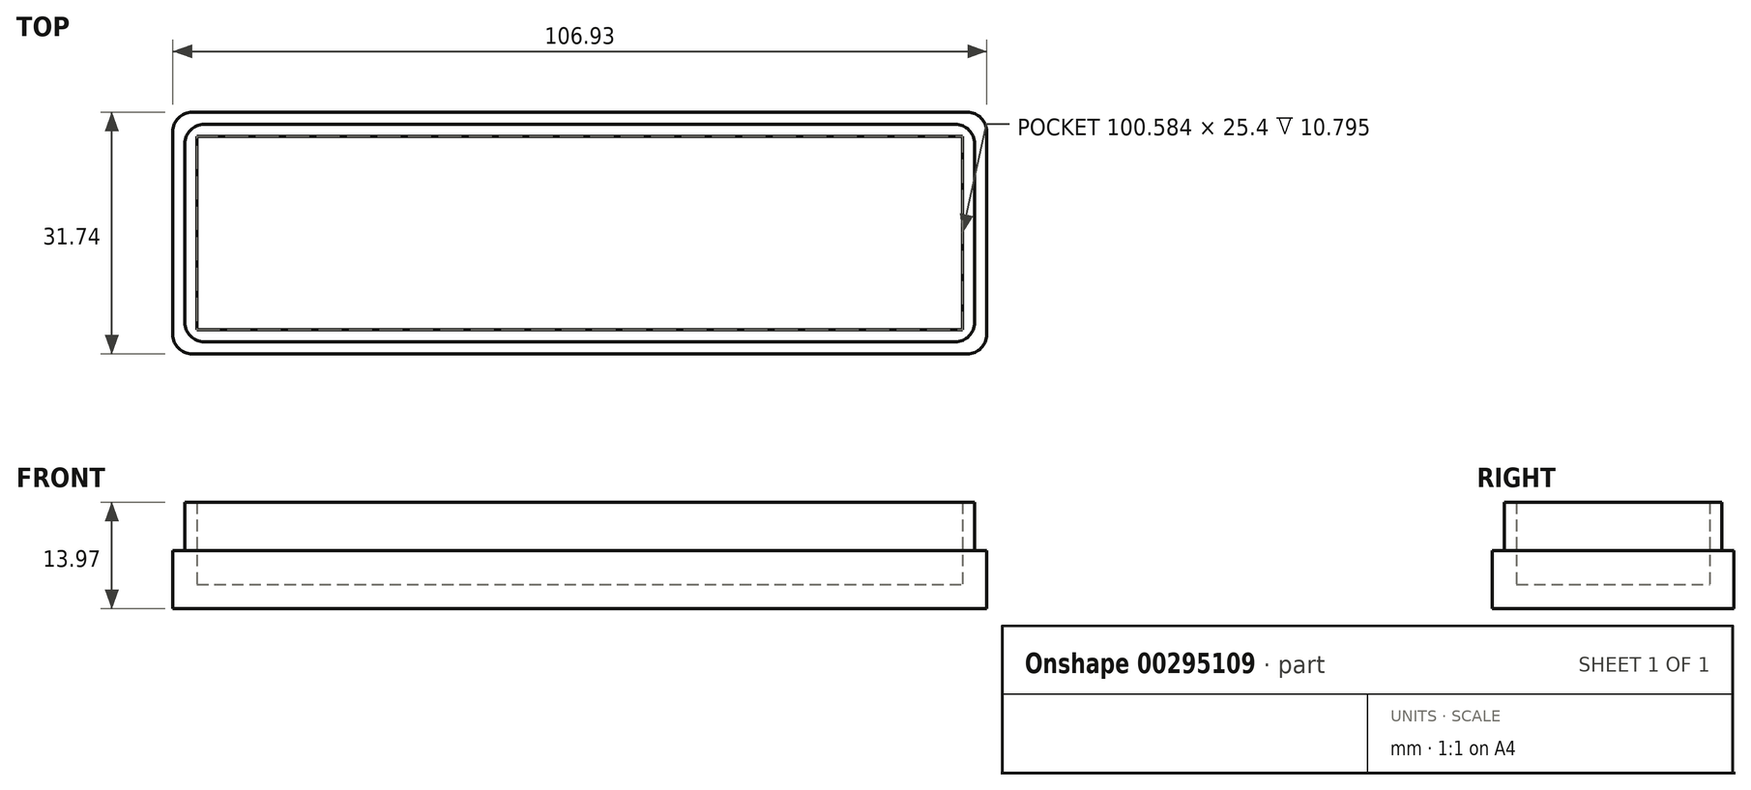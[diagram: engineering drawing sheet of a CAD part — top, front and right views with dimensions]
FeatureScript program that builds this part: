
annotation { "Feature Type Name" : "Feature", "Feature Type Description" : "" }
export const myFeature = defineFeature(function(context is Context, id is Id, definition is map)
    precondition{}
    {
        {
            var Q0;
            Q0=qCreatedBy(makeId("Top.planeOp"),FACE);
            var sketch = newSketch(context, id + "F0", { "sketchPlane" : qUnion([Q0])});
            skLineSegment(sketch, "E0.bottom", {"start": v(0, 0) * mm, "end": v(100.58, 0) * mm});
            skLineSegment(sketch, "E0.top", {"start": v(0, 25.4) * mm, "end": v(100.58, 25.4) * mm});
            skLineSegment(sketch, "E0.left", {"start": v(0, 0) * mm, "end": v(0, 25.4) * mm});
            skLineSegment(sketch, "E0.right", {"start": v(100.58, 0) * mm, "end": v(100.58, 25.4) * mm});
            skLineSegment(sketch, "E1.bottom", {"start": v(-3.18, 28.58) * mm, "end": v(103.76, 28.58) * mm});
            skLineSegment(sketch, "E1.top", {"start": v(-3.18, -3.18) * mm, "end": v(103.76, -3.18) * mm});
            skLineSegment(sketch, "E1.left", {"start": v(-3.18, 28.58) * mm, "end": v(-3.17, -3.18) * mm});
            skLineSegment(sketch, "E1.right", {"start": v(103.76, 28.58) * mm, "end": v(103.76, -3.18) * mm});
            skSolve(sketch);
        }
        {
            var Q0;
            Q0=makeQuery(id+"F0.imprint","IMPRINT",FACE,{"disambiguationData":[TD([[makeQuery(id+"F0.imprint","IMPRINT",EDGE,{"derivedFrom":sQuery(id+"F0.wireOp",EDGE,"E0.bottom")}),-1.0]])]});
            extrude(context, id + "F1", {"entities" : qUnion([Q0]), "depth" : 13.97 * mm});
        }
        {
            var Q0;
            Q0=makeQuery(id+"F0.imprint","IMPRINT",FACE,{"disambiguationData":[TD([[makeQuery(id+"F0.imprint","IMPRINT",EDGE,{"derivedFrom":sQuery(id+"F0.wireOp",EDGE,"E0.bottom")}),1.0]])]});
            extrude(context, id + "F2", {"entities" : qUnion([Q0]), "operationType" : NewBodyOperationType.ADD, "depth" : 3.17 * mm});
        }
        {
            var Q0;
            Q0=makeQuery(id+"F1.opExtrude","CAP_FACE",FACE,{"disambiguationData":[OSD([sQuery(id+"F0.wireOp",EDGE,"E0.bottom"),sQuery(id+"F0.wireOp",EDGE,"E0.top"),sQuery(id+"F0.wireOp",EDGE,"E0.left"),sQuery(id+"F0.wireOp",EDGE,"E0.right"),sQuery(id+"F0.wireOp",EDGE,"E1.bottom"),sQuery(id+"F0.wireOp",EDGE,"E1.top"),sQuery(id+"F0.wireOp",EDGE,"E1.left"),sQuery(id+"F0.wireOp",EDGE,"E1.right")])],"isStart":false});
            var sketch = newSketch(context, id + "F3", { "sketchPlane" : qUnion([Q0])});
            skLineSegment(sketch, "E2.bottom", {"start": v(-1.59, -1.59) * mm, "end": v(102.17, -1.59) * mm});
            skLineSegment(sketch, "E2.top", {"start": v(-1.59, 26.99) * mm, "end": v(102.17, 26.99) * mm});
            skLineSegment(sketch, "E2.left", {"start": v(-1.59, -1.59) * mm, "end": v(-1.59, 26.99) * mm});
            skLineSegment(sketch, "E2.right", {"start": v(102.17, -1.59) * mm, "end": v(102.17, 26.99) * mm});
            skSolve(sketch);
        }
        {
            var Q0;
            Q0=makeQuery(id+"F3.imprint","IMPRINT",FACE,{"disambiguationData":[TD([[makeQuery(id+"F3.imprint","IMPRINT",EDGE,{"derivedFrom":sQuery(id+"F3.wireOp",EDGE,"E2.bottom")}),-1.0]])]});
            extrude(context, id + "F4", {"entities" : qUnion([Q0]), "operationType" : NewBodyOperationType.REMOVE, "oppositeDirection" : true, "depth" : 6.35 * mm});
        }
        {
            var Q0;
            Q0=makeQuery(id+"F4.boolean.opBoolean","COPY",EDGE,{"derivedFrom":makeQuery(id+"F4.opExtrude","SWEPT_EDGE",EDGE,{"disambiguationData":[OSD([sQuery(id+"F3.wireOp",EDGE,"E2.bottom"),sQuery(id+"F3.wireOp",EDGE,"E2.left")])]})});
            var Q1;
            Q1=makeQuery(id+"F1.opExtrude","SWEPT_EDGE",EDGE,{"disambiguationData":[OSD([sQuery(id+"F0.wireOp",EDGE,"E1.top"),sQuery(id+"F0.wireOp",EDGE,"E1.left")])]});
            var Q2;
            Q2=makeQuery(id+"F4.boolean.opBoolean","COPY",EDGE,{"derivedFrom":makeQuery(id+"F4.opExtrude","SWEPT_EDGE",EDGE,{"disambiguationData":[OSD([sQuery(id+"F3.wireOp",EDGE,"E2.top"),sQuery(id+"F3.wireOp",EDGE,"E2.left")])]})});
            var Q3;
            Q3=makeQuery(id+"F1.opExtrude","SWEPT_EDGE",EDGE,{"disambiguationData":[OSD([sQuery(id+"F0.wireOp",EDGE,"E1.bottom"),sQuery(id+"F0.wireOp",EDGE,"E1.left")])]});
            var Q4;
            Q4=makeQuery(id+"F4.boolean.opBoolean","COPY",EDGE,{"derivedFrom":makeQuery(id+"F4.opExtrude","SWEPT_EDGE",EDGE,{"disambiguationData":[OSD([sQuery(id+"F3.wireOp",EDGE,"E2.bottom"),sQuery(id+"F3.wireOp",EDGE,"E2.right")])]})});
            var Q5;
            Q5=makeQuery(id+"F1.opExtrude","SWEPT_EDGE",EDGE,{"disambiguationData":[OSD([sQuery(id+"F0.wireOp",EDGE,"E1.top"),sQuery(id+"F0.wireOp",EDGE,"E1.right")])]});
            var Q6;
            Q6=makeQuery(id+"F1.opExtrude","SWEPT_EDGE",EDGE,{"disambiguationData":[OSD([sQuery(id+"F0.wireOp",EDGE,"E1.bottom"),sQuery(id+"F0.wireOp",EDGE,"E1.right")])]});
            var Q7;
            Q7=makeQuery(id+"F4.boolean.opBoolean","COPY",EDGE,{"derivedFrom":makeQuery(id+"F4.opExtrude","SWEPT_EDGE",EDGE,{"disambiguationData":[OSD([sQuery(id+"F3.wireOp",EDGE,"E2.top"),sQuery(id+"F3.wireOp",EDGE,"E2.right")])]})});
            fillet(context, id + "F5", {"entities" : qUnion([Q0, Q1, Q2, Q3, Q4, Q5, Q6, Q7]), "radius" : 2.54 * mm, "tangentPropagation" : true, "allowEdgeOverflow" : false});
        }
    });
